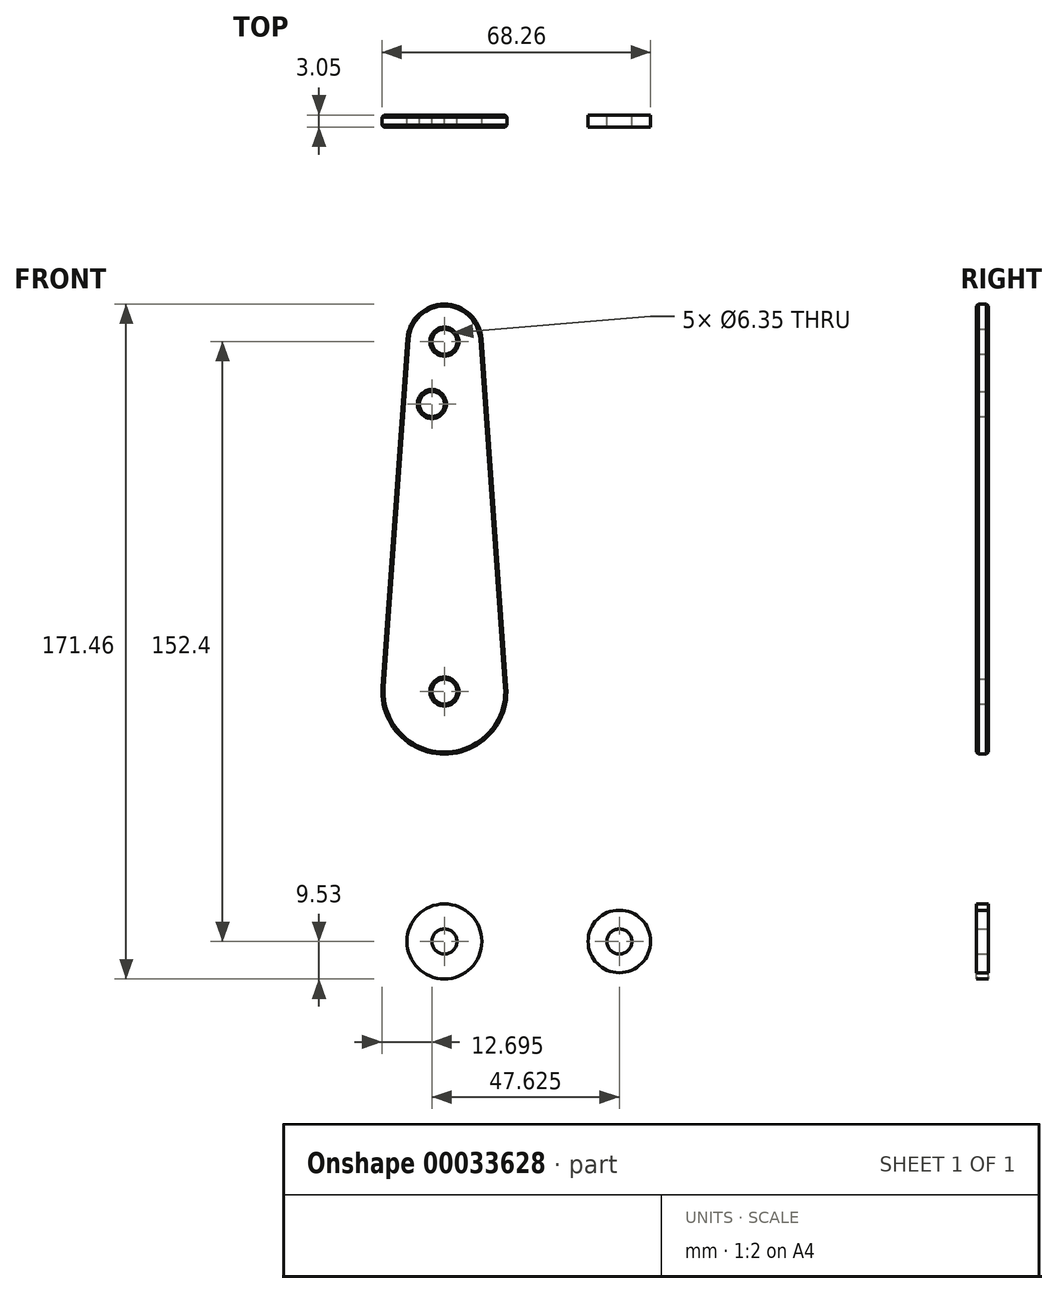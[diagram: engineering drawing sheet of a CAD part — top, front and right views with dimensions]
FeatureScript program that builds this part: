
annotation { "Feature Type Name" : "Feature", "Feature Type Description" : "" }
export const myFeature = defineFeature(function(context is Context, id is Id, definition is map)
    precondition{}
    {
        {
            var Q0;
            Q0=qCreatedBy(makeId("Front.planeOp"),FACE);
            var sketch = newSketch(context, id + "F0", { "sketchPlane" : qUnion([Q0])});
            skCircle(sketch, "E0", {"center": v(0, 0) * mm, "radius": 9.53 * mm});
            skCircle(sketch, "E1", {"center": v(0, 63.5) * mm, "radius": 15.88 * mm});
            skCircle(sketch, "E2", {"center": v(0, 152.4) * mm, "radius": 9.53 * mm});
            skCircle(sketch, "E3", {"center": v(44.45, 0) * mm, "radius": 7.94 * mm});
            skLineSegment(sketch, "E4", {"start": v(0, 0) * mm, "end": v(0, 152.4) * mm, "construction": true});
            skLineSegment(sketch, "E5", {"start": v(0, 0) * mm, "end": v(44.45, 0) * mm, "construction": true});
            skLineSegment(sketch, "E6", {"start": v(9.5, 153.08) * mm, "end": v(15.83, 64.63) * mm});
            skLineSegment(sketch, "E7.MirrorCS", {"start": v(-9.5, 153.08) * mm, "end": v(-15.83, 64.63) * mm});
            skLineSegment(sketch, "E8", {"start": v(15.8, 61.91) * mm, "end": v(11.34, 17.6) * mm});
            skLineSegment(sketch, "E9.MirrorCS", {"start": v(-15.8, 61.91) * mm, "end": v(-9.48, -0.95) * mm});
            skLineSegment(sketch, "E10", {"start": v(44.73, -7.93) * mm, "end": v(0.34, -9.52) * mm});
            skLineSegment(sketch, "E11.MirrorCS", {"start": v(44.73, 7.93) * mm, "end": v(18.97, 8.85) * mm});
            skCircle(sketch, "E12", {"center": v(0, 152.4) * mm, "radius": 3.18 * mm});
            skCircle(sketch, "E13", {"center": v(0, 63.5) * mm, "radius": 3.18 * mm});
            skCircle(sketch, "E14", {"center": v(0, 0) * mm, "radius": 3.18 * mm});
            skCircle(sketch, "E15", {"center": v(44.45, 0) * mm, "radius": 3.18 * mm});
            skCircle(sketch, "E16", {"center": v(-3.18, 136.55) * mm, "radius": 3.18 * mm});
            skPoint(sketch, "E17.newPointA", {"position": v(9.48, -0.95) * mm});
            skPoint(sketch, "E17.newPointB", {"position": v(0.34, 9.52) * mm});
            skArc(sketch, "E17.filletArc", {"start": v(11.34, 17.6) * mm, "mid": v(13.26, 11.57) * mm, "end": v(18.97, 8.85) * mm});
            skSolve(sketch);
        }
        {
            var Q0;
            Q0=makeQuery(id+"F0.imprint","IMPRINT",FACE,{"disambiguationData":[TD([[makeQuery(id+"F0.imprint","IMPRINT",EDGE,{"derivedFrom":sQuery(id+"F0.wireOp",EDGE,"E14")}),-1.0]])]});
            var Q1;
            Q1=makeQuery(id+"F0.imprint","IMPRINT",FACE,{"disambiguationData":[TD([[makeQuery(id+"F0.imprint","IMPRINT",EDGE,{"derivedFrom":sQuery(id+"F0.wireOp",EDGE,"E12")}),-1.0]])]});
            var Q2;
            Q2=makeQuery(id+"F0.imprint","IMPRINT",FACE,{"disambiguationData":[TD([[makeQuery(id+"F0.imprint","IMPRINT",EDGE,{"derivedFrom":sQuery(id+"F0.wireOp",EDGE,"E15")}),-1.0]])]});
            var Q3;
            {var subQ2=sQuery(id+"F0.wireOp",EDGE,"E8");Q3=makeQuery(id+"F0.imprint","IMPRINT",FACE,{"disambiguationData":[TD([[makeQuery(id+"F0.imprint","IMPRINT",EDGE,{"derivedFrom":subQ2}),-1.0]])]});}
            var Q4;
            Q4=makeQuery(id+"F0.imprint","IMPRINT",FACE,{"disambiguationData":[TD([[makeQuery(id+"F0.imprint","IMPRINT",EDGE,{"derivedFrom":sQuery(id+"F0.wireOp",EDGE,"E13")}),-1.0]])]});
            var Q5;
            {var subQ1=sQuery(id+"F0.wireOp",EDGE,"E6");Q5=makeQuery(id+"F0.imprint","IMPRINT",FACE,{"disambiguationData":[TD([[makeQuery(id+"F0.imprint","IMPRINT",EDGE,{"derivedFrom":subQ1}),-1.0]])]});}
            extrude(context, id + "F1", {"entities" : qUnion([Q0, Q1, Q2, Q3, Q4, Q5]), "depth" : 3.05 * mm});
        }
        {
            var Q0;
            Q0=makeQuery(id+"F1.opExtrude","CAP_FACE",FACE,{"disambiguationData":[OSD([sQuery(id+"F0.wireOp",EDGE,"E0"),sQuery(id+"F0.wireOp",EDGE,"E1"),sQuery(id+"F0.wireOp",EDGE,"E2"),sQuery(id+"F0.wireOp",EDGE,"E3"),sQuery(id+"F0.wireOp",EDGE,"E6"),sQuery(id+"F0.wireOp",EDGE,"E7.MirrorCS"),sQuery(id+"F0.wireOp",EDGE,"E8"),sQuery(id+"F0.wireOp",EDGE,"E9.MirrorCS"),sQuery(id+"F0.wireOp",EDGE,"E10"),sQuery(id+"F0.wireOp",EDGE,"E11.MirrorCS"),sQuery(id+"F0.wireOp",EDGE,"E12"),sQuery(id+"F0.wireOp",EDGE,"E13"),sQuery(id+"F0.wireOp",EDGE,"E14"),sQuery(id+"F0.wireOp",EDGE,"E15"),sQuery(id+"F0.wireOp",EDGE,"E16"),sQuery(id+"F0.wireOp",EDGE,"E17.filletArc")])],"isStart":false});
            chamfer(context, id + "F2", {"entities" : qUnion([Q0]), "width" : 0.5 * mm, "tangentPropagation" : true});
        }
        {
            var Q0;
            Q0=makeQuery(id+"F1.opExtrude","CAP_FACE",FACE,{"disambiguationData":[OSD([sQuery(id+"F0.wireOp",EDGE,"E0"),sQuery(id+"F0.wireOp",EDGE,"E1"),sQuery(id+"F0.wireOp",EDGE,"E2"),sQuery(id+"F0.wireOp",EDGE,"E3"),sQuery(id+"F0.wireOp",EDGE,"E6"),sQuery(id+"F0.wireOp",EDGE,"E7.MirrorCS"),sQuery(id+"F0.wireOp",EDGE,"E8"),sQuery(id+"F0.wireOp",EDGE,"E9.MirrorCS"),sQuery(id+"F0.wireOp",EDGE,"E10"),sQuery(id+"F0.wireOp",EDGE,"E11.MirrorCS"),sQuery(id+"F0.wireOp",EDGE,"E12"),sQuery(id+"F0.wireOp",EDGE,"E13"),sQuery(id+"F0.wireOp",EDGE,"E14"),sQuery(id+"F0.wireOp",EDGE,"E15"),sQuery(id+"F0.wireOp",EDGE,"E16"),sQuery(id+"F0.wireOp",EDGE,"E17.filletArc")])],"isStart":true});
            chamfer(context, id + "F3", {"entities" : qUnion([Q0]), "width" : 0.5 * mm, "tangentPropagation" : true});
        }
    });
